# Revit family: Beam_Clamp-Unistrut-P2898
name_source: partatom
category: Specialty Equipment
revit_build: Autodesk Revit Architecture 2012 (Build: 20110916_2132(x64)
units: mm (PartAtom-declared; Revit-internal decimal feet)

## types (5) — shared parameters
04 CSI = 26 05 48
95 CSI = 16070
Allowable Moment = 0.00 N-m
Assembly Code = D5020100
CAD URL = http://unistrut.us
Category = Specialty Equipment
Literature URL = http://unistrut.us
Load Capacity Note = Visit the product page for load application and capacity.
Manufacturer = Unistrut by Atkore International
Manufacturer Fax = 708-339-7814
Overall Length = 0"
Part Type = Beam Clamp
Product Page URL = http://unistrut.us
Subcategory = Beam Clamps
URL = http://unistrut.us
Unistrut Part Number = P2898-87
Unit = <By Category>
ecoScorecard Product Page = http://products.ecoscorecard.com
ecoScorecard_data = http://products.ecoscorecard.com

## per-type parameters (varying)
| type | A | B | D | E | F | Overall Height | Overall Width | Weight Per Piece |
| P2898-37 | 3/8" | 2" | 5/8" | 1 1/2" | 1" | 1 3/4" | 1 1/4" | 0.33 lb |
| P2898-50 | 1/2" | 1 5/16" | 1/2" | 1" | 3/4" | 1 1/2" | 7/8" | 0.33 lb |
| P2898-62 | 5/8" | 1 1/2" | 1/2" | 1" | 3/4" | 1 1/2" | 1" | 0.22 lb |
| P2898-75 | 3/4" | 1 7/8" | 5/8" | 1 3/8" | 1" | 1 3/4" | 1 1/4" | 0.88 lb |
| P2898-87 | 7/8" | 2" | 5/8" | 1 1/2" | 1" | 1 3/4" | 1 1/4" | 0.79 lb |

note: column(s) folded — value = type name in every type: Model

## geometry (parser evidence)
native form markers: Sweep x2
no freeform markers — native parametric forms only
